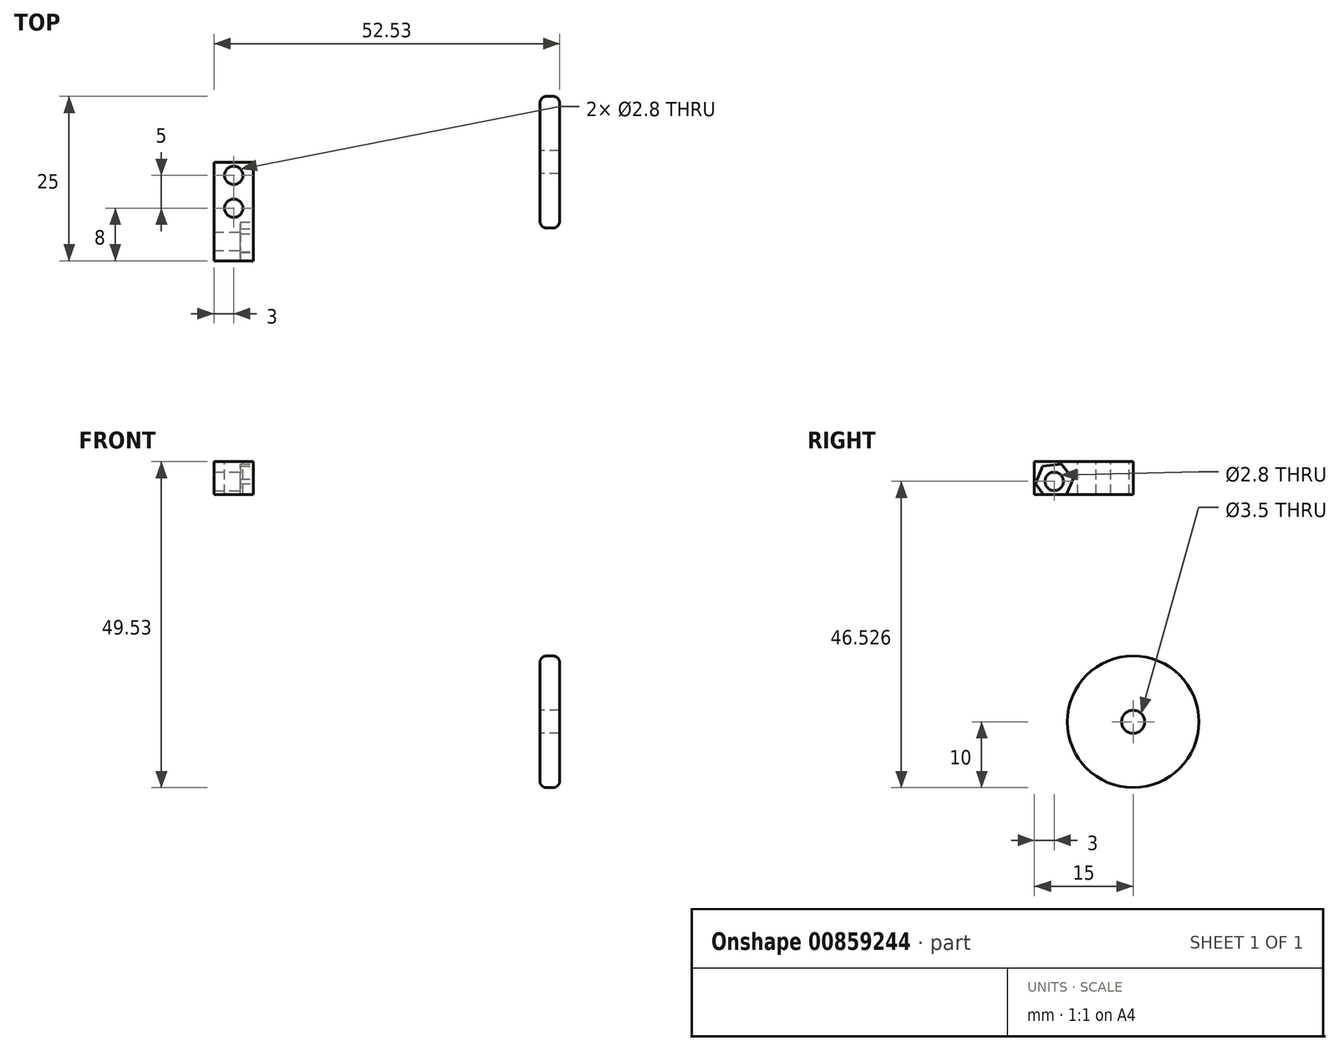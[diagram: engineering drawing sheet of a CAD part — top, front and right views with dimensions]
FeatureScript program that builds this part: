
annotation { "Feature Type Name" : "Feature", "Feature Type Description" : "" }
export const myFeature = defineFeature(function(context is Context, id is Id, definition is map)
    precondition{}
    {
        {
            var Q0;
            Q0=qCreatedBy(makeId("Right.planeOp"),FACE);
            var sketch = newSketch(context, id + "F0", { "sketchPlane" : qUnion([Q0])});
            skCircle(sketch, "E0", {"center": v(0, 0) * mm, "radius": 10 * mm});
            skSolve(sketch);
        }
        {
            var Q0;
            Q0=qSketchRegion(id+"F0",true);
            extrude(context, id + "F1", {"entities" : qUnion([Q0]), "endBound" : BoundingType.SYMMETRIC, "depth" : 3 * mm, "offsetDistance" : 25 * mm});
        }
        {
            var Q0;
            Q0=makeQuery(id+"F1.opExtrude","CAP_FACE",FACE,{"disambiguationData":[OSD([sQuery(id+"F0.wireOp",EDGE,"E0")])],"isStart":true});
            var sketch = newSketch(context, id + "F2", { "sketchPlane" : qUnion([Q0])});
            skCircle(sketch, "E1", {"center": v(0, 0) * mm, "radius": 1.75 * mm});
            skSolve(sketch);
        }
        {
            var Q0;
            Q0=qSketchRegion(id+"F2",true);
            extrude(context, id + "F3", {"entities" : qUnion([Q0]), "operationType" : NewBodyOperationType.REMOVE, "endBound" : BoundingType.THROUGH_ALL, "oppositeDirection" : true, "depth" : 25 * mm, "offsetDistance" : 25 * mm});
        }
        {
            var Q0;
            Q0=qCreatedBy(makeId("Front.planeOp"),FACE);
            var sketch = newSketch(context, id + "F4", { "sketchPlane" : qUnion([Q0])});
            skLineSegment(sketch, "E2.bottom", {"start": v(-51.03, 39.53) * mm, "end": v(-45.03, 39.53) * mm});
            skLineSegment(sketch, "E2.top", {"start": v(-51.03, 34.53) * mm, "end": v(-45.03, 34.53) * mm});
            skLineSegment(sketch, "E2.left", {"start": v(-51.03, 39.53) * mm, "end": v(-51.03, 34.53) * mm});
            skLineSegment(sketch, "E2.right", {"start": v(-45.03, 39.53) * mm, "end": v(-45.03, 34.53) * mm});
            skSolve(sketch);
        }
        {
            var Q0;
            Q0 = qSketchRegion(id + "F4", true);
            extrude(context, id + "F5", {"entities" : qUnion([Q0]), "depth" : 15 * mm, "offsetDistance" : 25 * mm});
        }
        {
            var Q0;
            Q0=makeQuery(id+"F5.opExtrude","SWEPT_FACE",FACE,{"disambiguationData":[OSD([sQuery(id+"F4.wireOp",EDGE,"E2.bottom")])]});
            var sketch = newSketch(context, id + "F6", { "sketchPlane" : qUnion([Q0])});
            skCircle(sketch, "E3", {"center": v(-48.03, -2) * mm, "radius": 1.4 * mm});
            skPoint(sketch, "E3.centerSnap0", {"position": v(-48.03, 0) * mm});
            skCircle(sketch, "E4", {"center": v(-48.03, -7) * mm, "radius": 1.4 * mm});
            skSolve(sketch);
        }
        {
            var Q0;
            Q0 = qSketchRegion(id + "F6", true);
            extrude(context, id + "F7", {"entities" : qUnion([Q0]), "operationType" : NewBodyOperationType.REMOVE, "endBound" : BoundingType.THROUGH_ALL, "oppositeDirection" : true, "depth" : 25 * mm, "offsetDistance" : 25 * mm});
        }
        {
            var Q0;
            Q0=makeQuery(id+"F5.opExtrude","SWEPT_FACE",FACE,{"disambiguationData":[OSD([sQuery(id+"F4.wireOp",EDGE,"E2.right")])]});
            var sketch = newSketch(context, id + "F8", { "sketchPlane" : qUnion([Q0])});
            skCircle(sketch, "E5", {"center": v(-12, 36.53) * mm, "radius": 1.4 * mm});
            skCircle(sketch, "E6.cCircle", {"center": v(-12, 36.53) * mm, "radius": 2.5 * mm, "construction": true});
            skLineSegment(sketch, "E6.0", {"start": v(-13.12, 33.86) * mm, "end": v(-14.86, 36.16) * mm});
            skLineSegment(sketch, "E6.1", {"start": v(-14.86, 36.16) * mm, "end": v(-13.75, 38.82) * mm});
            skLineSegment(sketch, "E6.2", {"start": v(-13.75, 38.82) * mm, "end": v(-10.88, 39.19) * mm});
            skLineSegment(sketch, "E6.3", {"start": v(-10.88, 39.19) * mm, "end": v(-9.14, 36.89) * mm});
            skLineSegment(sketch, "E6.4", {"start": v(-9.14, 36.89) * mm, "end": v(-10.25, 34.23) * mm});
            skLineSegment(sketch, "E6.5", {"start": v(-10.25, 34.23) * mm, "end": v(-13.12, 33.86) * mm});
            skPoint(sketch, "E6.0.midPoint", {"position": v(-14, 35.01) * mm});
            skSolve(sketch);
        }
        {
            var Q0;
            Q0=makeQuery(id+"F1.opExtrude","CAP_EDGE",EDGE,{"disambiguationData":[OSD([sQuery(id+"F0.wireOp",EDGE,"E0")])],"isStart":false});
            var Q1;
            Q1=makeQuery(id+"F1.opExtrude","CAP_EDGE",EDGE,{"disambiguationData":[OSD([sQuery(id+"F0.wireOp",EDGE,"E0")])],"isStart":true});
            fillet(context, id + "F9", {"entities" : qUnion([Q0, Q1]), "radius" : 1 * mm, "tangentPropagation" : true, "allowEdgeOverflow" : false});
        }
        {
            var Q0;
            Q0=makeQuery(id+"F8.imprint","IMPRINT",FACE,{"disambiguationData":[TD([[makeQuery(id+"F8.imprint","IMPRINT",EDGE,{"derivedFrom":sQuery(id+"F8.wireOp",EDGE,"E5")}),1.0]])]});
            extrude(context, id + "F10", {"entities" : qUnion([Q0]), "operationType" : NewBodyOperationType.REMOVE, "endBound" : BoundingType.THROUGH_ALL, "oppositeDirection" : true, "depth" : 25 * mm, "offsetDistance" : 25 * mm});
        }
        {
            var Q0;
            Q0=makeQuery(id+"F8.imprint","IMPRINT",FACE,{"disambiguationData":[TD([[makeQuery(id+"F8.imprint","IMPRINT",EDGE,{"derivedFrom":sQuery(id+"F8.wireOp",EDGE,"E5")}),-1.0]])]});
            extrude(context, id + "F11", {"entities" : qUnion([Q0]), "operationType" : NewBodyOperationType.REMOVE, "oppositeDirection" : true, "depth" : 2 * mm, "offsetDistance" : 25 * mm});
        }
    });
